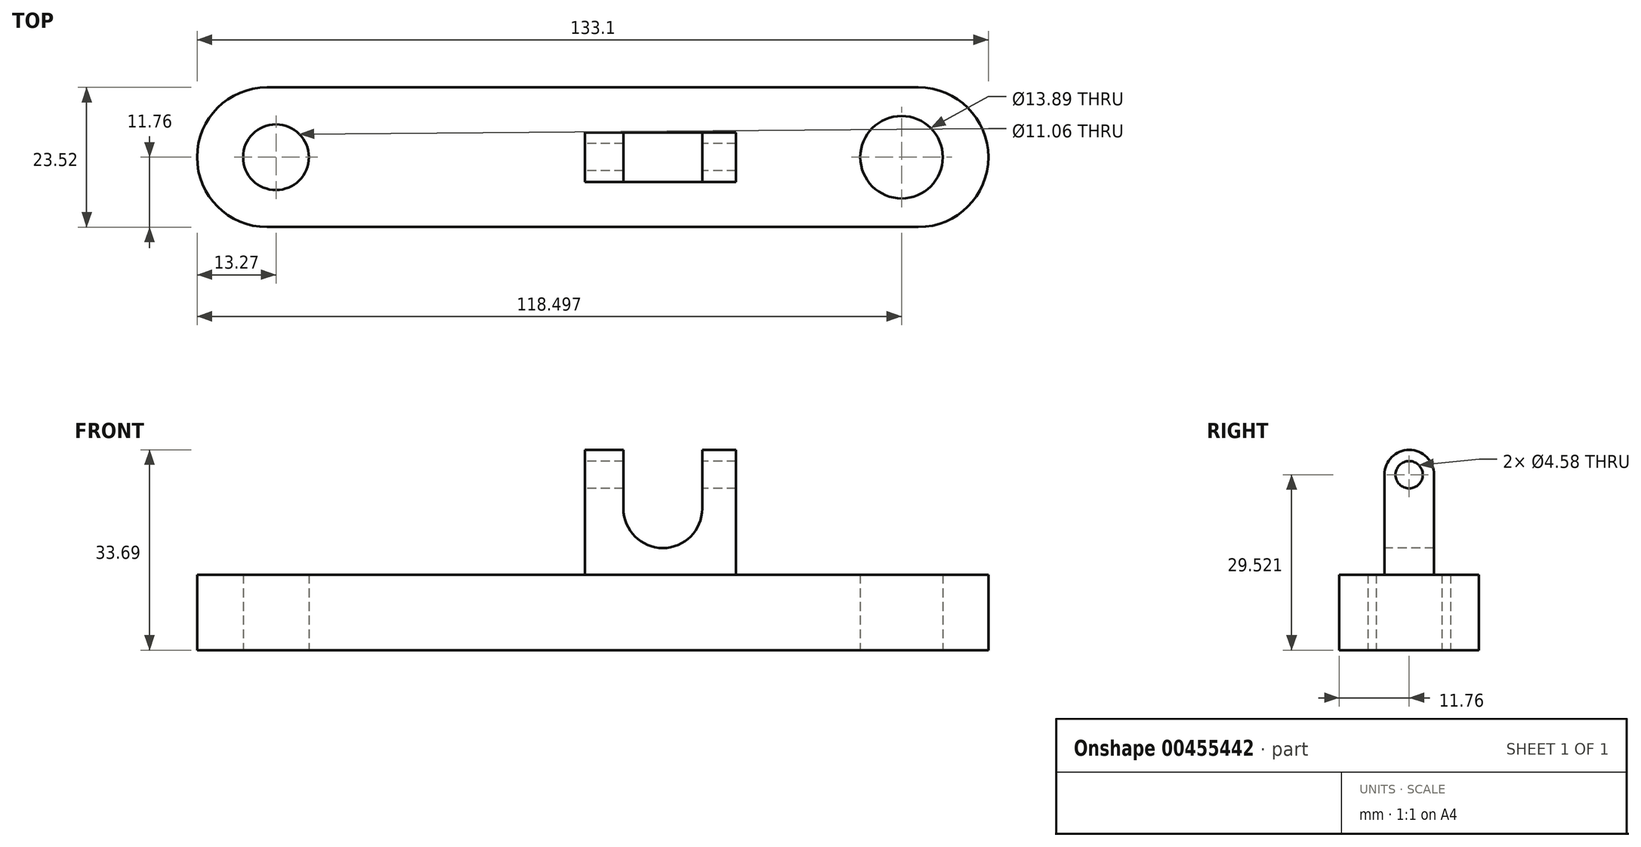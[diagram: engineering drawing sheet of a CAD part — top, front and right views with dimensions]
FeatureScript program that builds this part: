
annotation { "Feature Type Name" : "Feature", "Feature Type Description" : "" }
export const myFeature = defineFeature(function(context is Context, id is Id, definition is map)
    precondition{}
    {
        {
            var Q0;
            Q0=qCreatedBy(makeId("Top.planeOp"),FACE);
            var sketch = newSketch(context, id + "F0", { "sketchPlane" : qUnion([Q0])});
            skLineSegment(sketch, "E0.bottom", {"start": v(56.12, -11.76) * mm, "end": v(-53.47, -11.76) * mm});
            skLineSegment(sketch, "E0.top", {"start": v(56.12, 11.76) * mm, "end": v(-53.47, 11.76) * mm});
            skLineSegment(sketch, "E0.left", {"start": v(56.12, -11.76) * mm, "end": v(56.12, 11.76) * mm});
            skLineSegment(sketch, "E0.right", {"start": v(-53.47, -11.76) * mm, "end": v(-53.47, 11.76) * mm});
            skPoint(sketch, "E0.middle", {"position": v(1.33, 0) * mm});
            skArc(sketch, "E1", {"start": v(-53.47, 11.76) * mm, "mid": v(-65.22, 0) * mm, "end": v(-53.47, -11.76) * mm});
            skArc(sketch, "E2", {"start": v(56.12, 11.76) * mm, "mid": v(67.88, 0) * mm, "end": v(56.12, -11.76) * mm});
            skCircle(sketch, "E3", {"center": v(-51.95, 0) * mm, "radius": 5.53 * mm});
            skCircle(sketch, "E4", {"center": v(53.28, 0) * mm, "radius": 6.94 * mm});
            skSolve(sketch);
        }
        {
            var Q0;
            Q0 = qSketchRegion(id + "F0", true);
            extrude(context, id + "F1", {"entities" : qUnion([Q0]), "depth" : 12.7 * mm});
        }
        {
            var Q0;
            Q0=qCreatedBy(makeId("Right.planeOp"),FACE);
            var sketch = newSketch(context, id + "F2", { "sketchPlane" : qUnion([Q0])});
            skLineSegment(sketch, "E5.bottom", {"start": v(-4.17, 11.19) * mm, "end": v(4.17, 11.19) * mm});
            skLineSegment(sketch, "E5.top", {"start": v(-4.17, 29.52) * mm, "end": v(4.17, 29.52) * mm});
            skLineSegment(sketch, "E5.left", {"start": v(-4.17, 11.19) * mm, "end": v(-4.17, 29.52) * mm});
            skLineSegment(sketch, "E5.right", {"start": v(4.17, 11.19) * mm, "end": v(4.17, 29.52) * mm});
            skCircle(sketch, "E6", {"center": v(0, 29.52) * mm, "radius": 4.17 * mm});
            skCircle(sketch, "E7", {"center": v(0, 29.52) * mm, "radius": 2.3 * mm});
            skSolve(sketch);
        }
        {
            var Q0;
            Q0=makeQuery(id+"F2.imprint","IMPRINT",FACE,{"disambiguationData":[TD([[makeQuery(id+"F2.imprint","IMPRINT",EDGE,{"derivedFrom":sQuery(id+"F2.wireOp",EDGE,"E5.bottom")}),1.0]])]});
            var Q1;
            {var subQ1=sQuery(id+"F2.wireOp",EDGE,"E5.top");var subQ3=sQuery(id+"F2.wireOp",EDGE,"E7");var subQ4=makeQuery(id+"F2.imprint","INTERSECT",VERTEX,{"disambiguationData":[OD(0.0)],"derivedFrom":[subQ1,subQ3]});Q1=makeQuery(id+"F2.imprint","IMPRINT",FACE,{"disambiguationData":[TD([[makeQuery(id+"F2.imprint","IMPRINT",EDGE,{"disambiguationData":[TD([[subQ4,-1.0]])],"derivedFrom":subQ3}),-1.0]])]});}
            var Q2;
            {var subQ1=sQuery(id+"F2.wireOp",EDGE,"E5.top");var subQ3=sQuery(id+"F2.wireOp",EDGE,"E7");var subQ4=makeQuery(id+"F2.imprint","INTERSECT",VERTEX,{"disambiguationData":[OD(0.0)],"derivedFrom":[subQ1,subQ3]});Q2=makeQuery(id+"F2.imprint","IMPRINT",FACE,{"disambiguationData":[TD([[makeQuery(id+"F2.imprint","IMPRINT",EDGE,{"disambiguationData":[TD([[subQ4,1.0]])],"derivedFrom":subQ3}),-1.0]])]});}
            extrude(context, id + "F3", {"entities" : qUnion([Q0, Q1, Q2]), "operationType" : NewBodyOperationType.ADD, "depth" : 25.4 * mm});
        }
        {
            var Q0;
            Q0=makeQuery(id+"F3.opExtrude","SWEPT_FACE",FACE,{"disambiguationData":[OSD([sQuery(id+"F2.wireOp",EDGE,"E5.left")])]});
            var sketch = newSketch(context, id + "F4", { "sketchPlane" : qUnion([Q0])});
            skLineSegment(sketch, "E8", {"start": v(6.5, 33.73) * mm, "end": v(19.74, 33.73) * mm});
            skLineSegment(sketch, "E9", {"start": v(19.74, 33.73) * mm, "end": v(19.74, 23.8) * mm});
            skLineSegment(sketch, "E10", {"start": v(19.74, 23.8) * mm, "end": v(6.5, 23.8) * mm});
            skLineSegment(sketch, "E11", {"start": v(6.5, 23.8) * mm, "end": v(6.5, 33.78) * mm});
            skArc(sketch, "E12", {"start": v(19.74, 23.8) * mm, "mid": v(13.12, 17.18) * mm, "end": v(6.5, 23.8) * mm});
            skSolve(sketch);
        }
        {
            var Q0;
            Q0 = qSketchRegion(id + "F4", true);
            extrude(context, id + "F5", {"entities" : qUnion([Q0]), "operationType" : NewBodyOperationType.REMOVE, "endBound" : BoundingType.THROUGH_ALL, "oppositeDirection" : true, "depth" : 25.4 * mm});
        }
    });
